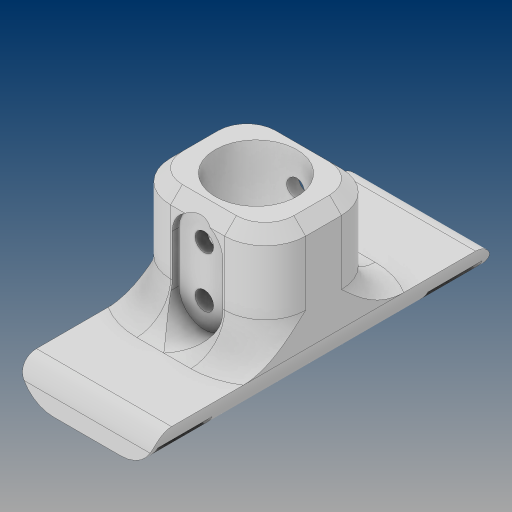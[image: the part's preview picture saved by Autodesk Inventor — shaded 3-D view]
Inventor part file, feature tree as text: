
AUTODESK INVENTOR PART (.ipt)
format: ipt  version: 2023 (Build 270158000, 158)  size: 616,448 bytes
history: native  units: mm
features: extrude x9, sketch x5, fillet x3, mirror x2, plane x1, chamfer x1
ambient origin geometry x8: Origin, YZ Plane, XZ Plane, XY Plane, X Axis, Y Axis, Z Axis, Center Point
bodies: Solid1 (feature_tree)
feature tree (21):
  sketch  "Sketch1"  dims[d0=50.0mm d1=100.0mm d2=300.0mm d3=20.0mm d4=10.0mm d5=2.0mm d6=0.5mm d7=0.5mm d8=70.0mm d9=15.0mm d10=15.0mm d11=15.0mm d12=15.0mm d13=12.8mm d14=12.8mm d15=12.8mm d16=1.0mm d17=1.0mm d18=2.0mm d19=30.0mm d20=2.0mm d21=30.0mm d22=2.0mm d23=40.595mm d24=2.5mm d25=30.0deg d26=60.0deg d27=220.451928mm d28=1.1mm d29=12.632665mm d30=120.0deg d31=20.0mm d32=0.0mm]
  extrude  "Extrusion1"  Depth=20.0mm TaperAngle=0.0deg
  extrude  "Extrusion2"  Depth=7.5mm
  sketch  "Sketch2"  dims[d33=7.5mm d34=0.0mm d35=7.5mm]
  extrude  "Extrusion3"  Depth=15.0mm
  extrude  "Extrusion4"  Depth=5.5mm
  plane  "Work Plane1"
  mirror  "Mirror1"
  mirror  "Mirror2"
  fillet  "Fillet1"  Radius=5.5mm
  sketch  "Sketch3"  dims[d36=7.5mm d37=15.0mm]
  extrude  "Extrusion5"  Depth=12.0mm TaperAngle=0.0deg
  extrude  "Extrusion6"  Depth=12.0mm
  sketch  "Sketch4"  dims[d38=15.0mm d39=5.5mm d40=5.5mm]
  extrude  "Extrusion7"  Depth=18.5mm
  fillet  "Fillet2"  Radius=8.0mm
  fillet  "Fillet3"  Radius=50.0mm
  chamfer  "Chamfer1"  Distance=19.5mm
  extrude  "Extrusion8"  Depth=24.15mm
  extrude  "Extrusion9"  Depth=2.1mm TaperAngle=0.0deg
  sketch  "Sketch5"  dims[d41=2.0mm d42=0.0mm d43=12.0mm d44=0.0mm d45=12.0mm d46=18.5mm d47=8.0mm d48=50.0mm d49=0.0mm d50=19.5mm d51=0.0mm d52=24.15mm d53=2.1mm d54=0.0mm d55=10.0mm d56=5.0mm d57=3.5mm d58=2.0mm d59=45.0deg d60=0.2mm d61=0.0mm d62=30.0mm d63=0.0mm]
